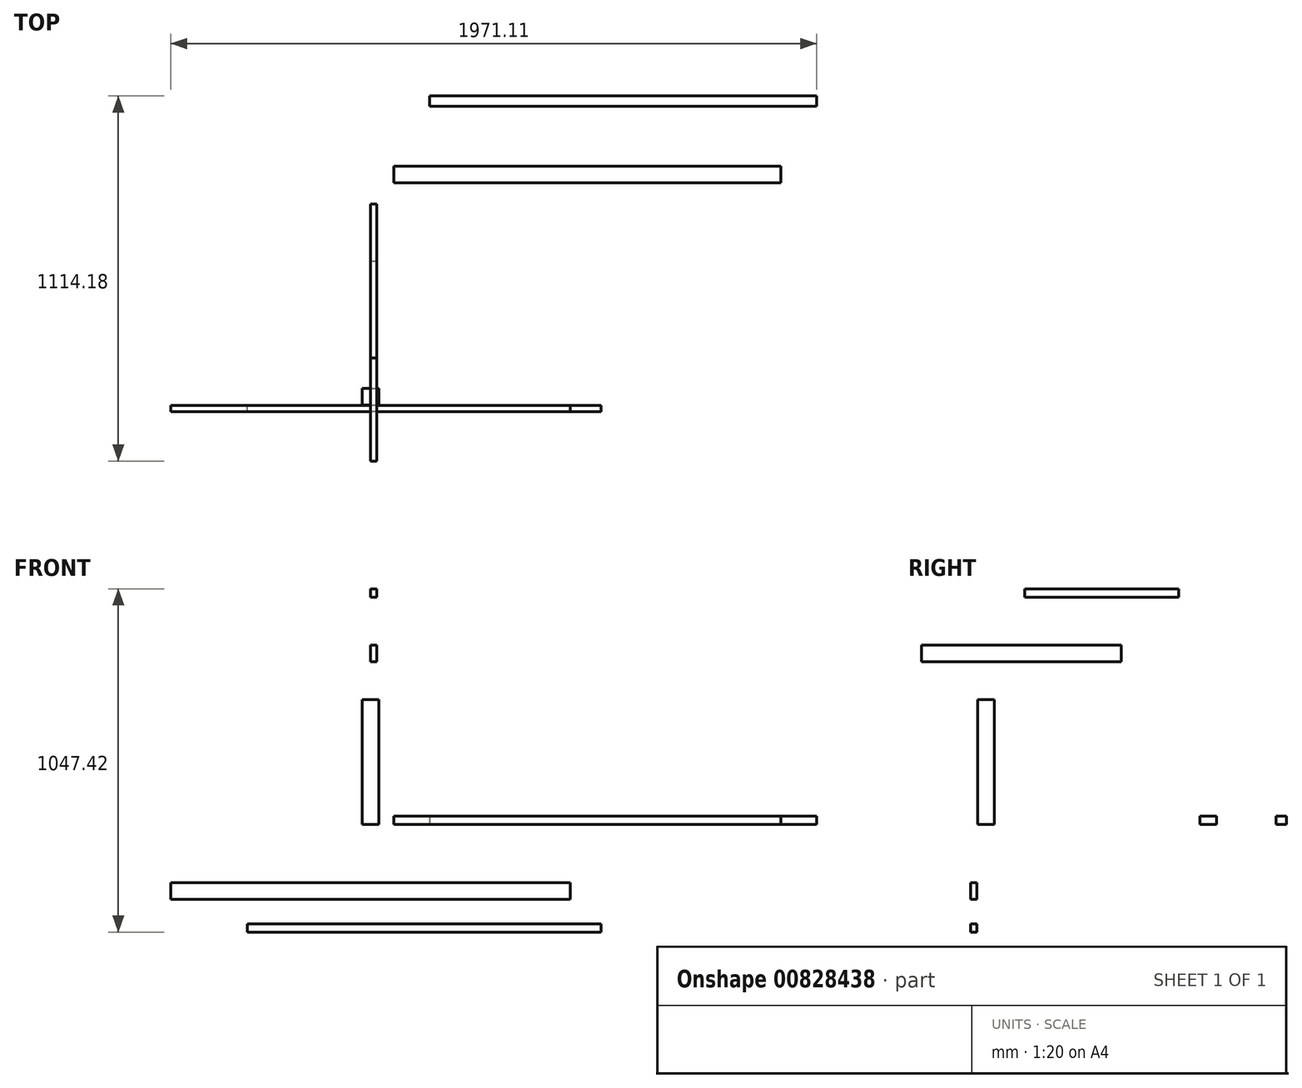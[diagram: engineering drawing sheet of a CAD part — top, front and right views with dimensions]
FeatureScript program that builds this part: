
annotation { "Feature Type Name" : "Feature", "Feature Type Description" : "" }
export const myFeature = defineFeature(function(context is Context, id is Id, definition is map)
    precondition{}
    {
        {
            var Q0;
            Q0=qCreatedBy(makeId("Top.planeOp"),FACE);
            var sketch = newSketch(context, id + "F0", { "sketchPlane" : qUnion([Q0])});
            skLineSegment(sketch, "E0.bottom", {"start": v(-25.4, 52.58) * mm, "end": v(25.4, 52.58) * mm});
            skLineSegment(sketch, "E0.top", {"start": v(-25.4, 1.78) * mm, "end": v(25.4, 1.78) * mm});
            skLineSegment(sketch, "E0.left", {"start": v(-25.4, 52.58) * mm, "end": v(-25.4, 1.78) * mm});
            skLineSegment(sketch, "E0.right", {"start": v(25.4, 52.58) * mm, "end": v(25.4, 1.78) * mm});
            skPoint(sketch, "E0.middle", {"position": v(0, 27.18) * mm});
            skSolve(sketch);
        }
        {
            var Q0;
            Q0 = qSketchRegion(id + "F0", true);
            extrude(context, id + "F1", {"entities" : qUnion([Q0]), "depth" : 381 * mm, "offsetDistance" : 25.4 * mm});
        }
        {
            var Q0;
            Q0=qCreatedBy(makeId("Front.planeOp"),FACE);
            var sketch = newSketch(context, id + "F2", { "sketchPlane" : qUnion([Q0])});
            skLineSegment(sketch, "E1.bottom", {"start": v(609.6, -177.4) * mm, "end": v(-609.6, -177.4) * mm});
            skLineSegment(sketch, "E1.top", {"start": v(609.6, -228.2) * mm, "end": v(-609.6, -228.2) * mm});
            skLineSegment(sketch, "E1.left", {"start": v(609.6, -177.4) * mm, "end": v(609.6, -228.2) * mm});
            skLineSegment(sketch, "E1.right", {"start": v(-609.6, -177.4) * mm, "end": v(-609.6, -228.2) * mm});
            skPoint(sketch, "E1.middle", {"position": v(0, -202.8) * mm});
            skSolve(sketch);
        }
        {
            var Q0;
            Q0 = qSketchRegion(id + "F2", true);
            extrude(context, id + "F3", {"entities" : qUnion([Q0]), "depth" : 19.05 * mm, "offsetDistance" : 25.4 * mm});
        }
        {
            var Q0;
            Q0=qCreatedBy(makeId("Right.planeOp"),FACE);
            var sketch = newSketch(context, id + "F4", { "sketchPlane" : qUnion([Q0])});
            skLineSegment(sketch, "E2.bottom", {"start": v(440.18, 548.03) * mm, "end": v(-169.42, 548.03) * mm});
            skLineSegment(sketch, "E2.top", {"start": v(440.18, 497.23) * mm, "end": v(-169.42, 497.23) * mm});
            skLineSegment(sketch, "E2.left", {"start": v(440.18, 548.03) * mm, "end": v(440.18, 497.23) * mm});
            skLineSegment(sketch, "E2.right", {"start": v(-169.42, 548.03) * mm, "end": v(-169.42, 497.23) * mm});
            skPoint(sketch, "E2.middle", {"position": v(135.38, 522.63) * mm});
            skSolve(sketch);
        }
        {
            var Q0;
            Q0 = qSketchRegion(id + "F4", true);
            extrude(context, id + "F5", {"entities" : qUnion([Q0]), "depth" : 19.05 * mm, "offsetDistance" : 25.4 * mm});
        }
        {
            var Q0;
            Q0=qCreatedBy(makeId("Right.planeOp"),FACE);
            var sketch = newSketch(context, id + "F6", { "sketchPlane" : qUnion([Q0])});
            skLineSegment(sketch, "E3.bottom", {"start": v(615.72, 694) * mm, "end": v(145.82, 694) * mm});
            skLineSegment(sketch, "E3.top", {"start": v(615.72, 719.4) * mm, "end": v(145.82, 719.4) * mm});
            skLineSegment(sketch, "E3.left", {"start": v(615.72, 694) * mm, "end": v(615.72, 719.4) * mm});
            skLineSegment(sketch, "E3.right", {"start": v(145.82, 694) * mm, "end": v(145.82, 719.4) * mm});
            skPoint(sketch, "E3.middle", {"position": v(380.77, 706.7) * mm});
            skSolve(sketch);
        }
        {
            var Q0;
            Q0=makeQuery(id+"F6.imprint","IMPRINT",FACE,{"disambiguationData":[TD([[makeQuery(id+"F6.imprint","IMPRINT",EDGE,{"derivedFrom":sQuery(id+"F6.wireOp",EDGE,"E3.bottom")}),-1.0]])]});
            var Q1;
            Q1 = qSketchRegion(id + "F6", true);
            extrude(context, id + "F7", {"entities" : qUnion([Q0, Q1]), "depth" : 19.05 * mm, "offsetDistance" : 25.4 * mm});
        }
        {
            var Q0;
            Q0=qCreatedBy(makeId("Front.planeOp"),FACE);
            var sketch = newSketch(context, id + "F8", { "sketchPlane" : qUnion([Q0])});
            skLineSegment(sketch, "E4.bottom", {"start": v(703.56, -302.62) * mm, "end": v(-375.94, -302.62) * mm});
            skLineSegment(sketch, "E4.top", {"start": v(703.56, -328.02) * mm, "end": v(-375.94, -328.02) * mm});
            skLineSegment(sketch, "E4.left", {"start": v(703.56, -302.62) * mm, "end": v(703.56, -328.02) * mm});
            skLineSegment(sketch, "E4.right", {"start": v(-375.94, -302.62) * mm, "end": v(-375.94, -328.02) * mm});
            skPoint(sketch, "E4.middle", {"position": v(163.8, -315.32) * mm});
            skSolve(sketch);
        }
        {
            var Q0;
            Q0 = qSketchRegion(id + "F8", true);
            extrude(context, id + "F9", {"entities" : qUnion([Q0]), "depth" : 19.05 * mm, "offsetDistance" : 25.4 * mm});
        }
        {
            var Q0;
            Q0=qCreatedBy(makeId("Top.planeOp"),FACE);
            var sketch = newSketch(context, id + "F10", { "sketchPlane" : qUnion([Q0])});
            skLineSegment(sketch, "E5.bottom", {"start": v(1251.94, 730.9) * mm, "end": v(70.84, 730.9) * mm});
            skLineSegment(sketch, "E5.top", {"start": v(1251.94, 680.1) * mm, "end": v(70.84, 680.1) * mm});
            skLineSegment(sketch, "E5.left", {"start": v(1251.94, 730.9) * mm, "end": v(1251.94, 680.1) * mm});
            skLineSegment(sketch, "E5.right", {"start": v(70.84, 730.9) * mm, "end": v(70.84, 680.1) * mm});
            skPoint(sketch, "E5.middle", {"position": v(661.4, 705.5) * mm});
            skSolve(sketch);
        }
        {
            var Q0;
            Q0 = qSketchRegion(id + "F10", true);
            extrude(context, id + "F11", {"entities" : qUnion([Q0]), "depth" : 25.4 * mm, "offsetDistance" : 25.4 * mm});
        }
        {
            var Q0;
            Q0=qCreatedBy(makeId("Top.planeOp"),FACE);
            var sketch = newSketch(context, id + "F12", { "sketchPlane" : qUnion([Q0])});
            skLineSegment(sketch, "E6.bottom", {"start": v(1361.5, 944.76) * mm, "end": v(180.4, 944.76) * mm});
            skLineSegment(sketch, "E6.top", {"start": v(1361.5, 913.01) * mm, "end": v(180.4, 913.01) * mm});
            skLineSegment(sketch, "E6.left", {"start": v(1361.5, 944.76) * mm, "end": v(1361.5, 913.01) * mm});
            skLineSegment(sketch, "E6.right", {"start": v(180.4, 944.76) * mm, "end": v(180.4, 913.01) * mm});
            skPoint(sketch, "E6.middle", {"position": v(770.96, 928.89) * mm});
            skSolve(sketch);
        }
        {
            var Q0;
            Q0 = qSketchRegion(id + "F12", true);
            extrude(context, id + "F13", {"entities" : qUnion([Q0]), "depth" : 25.4 * mm, "offsetDistance" : 25.4 * mm});
        }
    });
